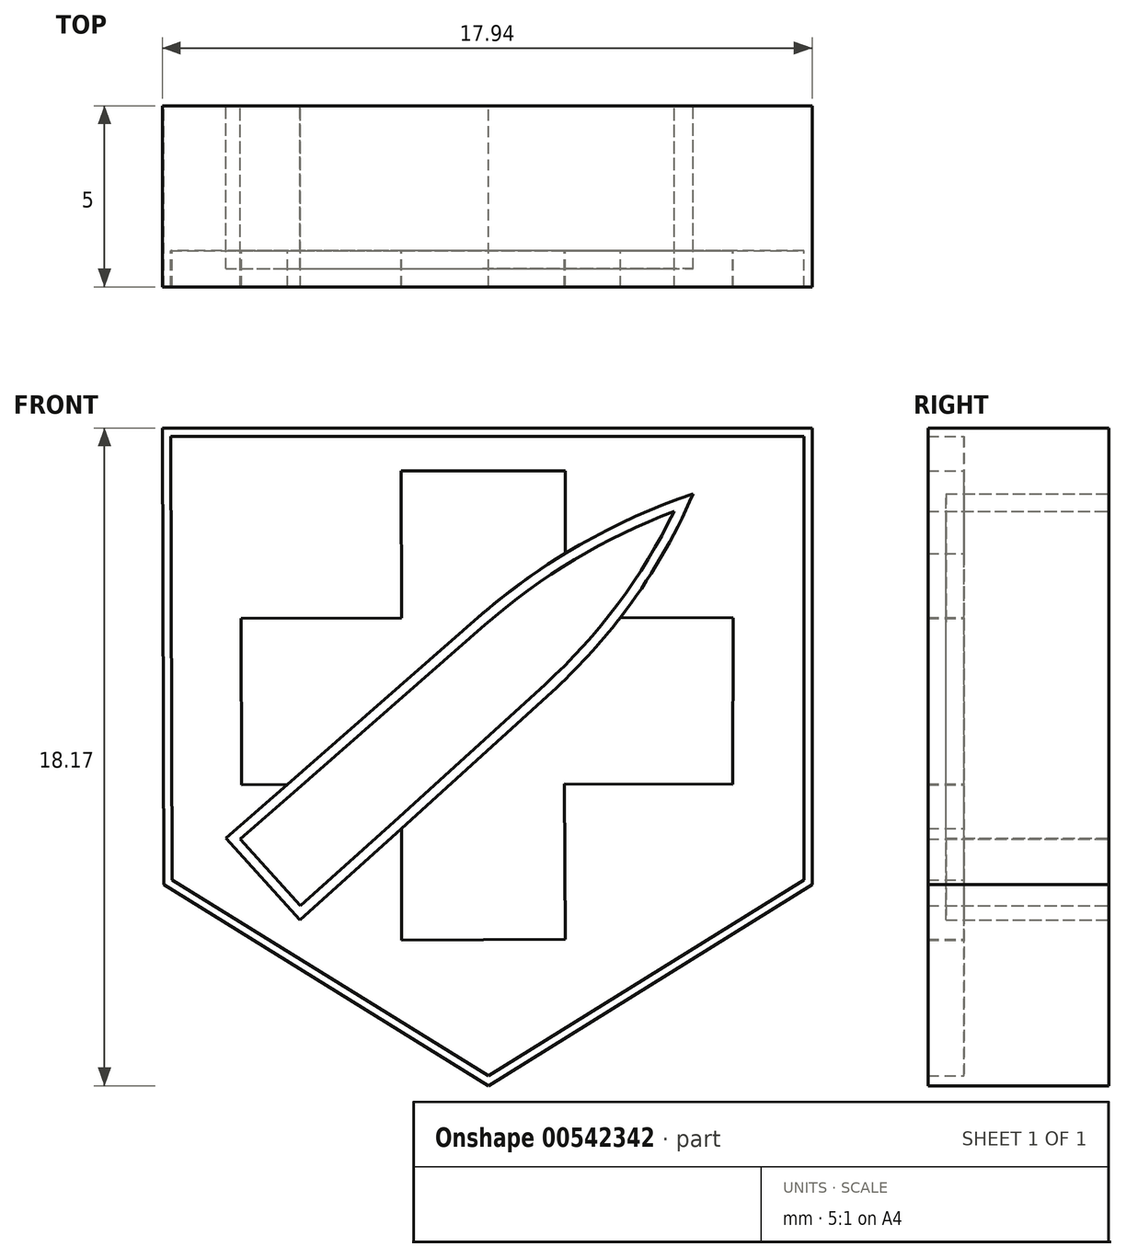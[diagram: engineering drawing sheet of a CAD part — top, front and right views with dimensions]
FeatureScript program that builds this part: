
annotation { "Feature Type Name" : "Feature", "Feature Type Description" : "" }
export const myFeature = defineFeature(function(context is Context, id is Id, definition is map)
    precondition{}
    {
        {
            var Q0;
            Q0=qCreatedBy(makeId("Front.planeOp"),FACE);
            var sketch = newSketch(context, id + "F0", { "sketchPlane" : qUnion([Q0])});
            skLineSegment(sketch, "E0", {"start": v(-10.75, 10.44) * mm, "end": v(7.2, 10.44) * mm});
            skLineSegment(sketch, "E1", {"start": v(7.2, 10.44) * mm, "end": v(7.2, -2.18) * mm});
            skLineSegment(sketch, "E2", {"start": v(7.2, -2.18) * mm, "end": v(-1.75, -7.73) * mm});
            skLineSegment(sketch, "E3", {"start": v(-1.75, -7.73) * mm, "end": v(-10.7, -2.18) * mm});
            skLineSegment(sketch, "E4", {"start": v(-10.7, -2.18) * mm, "end": v(-10.75, 10.44) * mm});
            skLineSegment(sketch, "E5.0", {"start": v(-10.52, 10.22) * mm, "end": v(6.96, 10.22) * mm});
            skLineSegment(sketch, "E5.1", {"start": v(-10.48, -2.05) * mm, "end": v(-10.52, 10.22) * mm});
            skLineSegment(sketch, "E5.2", {"start": v(6.96, 10.22) * mm, "end": v(6.96, -2.05) * mm});
            skLineSegment(sketch, "E5.3", {"start": v(6.96, -2.05) * mm, "end": v(-1.75, -7.46) * mm});
            skLineSegment(sketch, "E5.4", {"start": v(-1.75, -7.46) * mm, "end": v(-10.48, -2.05) * mm});
            skLineSegment(sketch, "E6", {"start": v(-4.17, 9.25) * mm, "end": v(-4.15, 5.2) * mm});
            skLineSegment(sketch, "E7", {"start": v(-4.15, 5.2) * mm, "end": v(-8.58, 5.18) * mm});
            skLineSegment(sketch, "E8", {"start": v(-8.58, 5.18) * mm, "end": v(-8.56, 0.59) * mm});
            skLineSegment(sketch, "E9", {"start": v(-8.56, 0.59) * mm, "end": v(-7.3, 0.6) * mm});
            skLineSegment(sketch, "E10", {"start": v(-7.3, 0.6) * mm, "end": v(-4.15, 0.6) * mm});
            skLineSegment(sketch, "E11", {"start": v(-4.15, -3.7) * mm, "end": v(-4.15, 0.6) * mm});
            skLineSegment(sketch, "E12", {"start": v(-4.15, -3.7) * mm, "end": v(0.37, -3.69) * mm});
            skLineSegment(sketch, "E13", {"start": v(0.37, -3.69) * mm, "end": v(0.35, 0.6) * mm});
            skLineSegment(sketch, "E14", {"start": v(0.35, 0.6) * mm, "end": v(5, 0.6) * mm});
            skLineSegment(sketch, "E15", {"start": v(5, 0.6) * mm, "end": v(5, 5.2) * mm});
            skLineSegment(sketch, "E16", {"start": v(5, 5.2) * mm, "end": v(0.37, 5.2) * mm});
            skLineSegment(sketch, "E17", {"start": v(0.37, 5.2) * mm, "end": v(0.37, 9.25) * mm});
            skLineSegment(sketch, "E18", {"start": v(0.37, 9.25) * mm, "end": v(-4.17, 9.25) * mm});
            skLineSegment(sketch, "E19", {"start": v(-9, -0.89) * mm, "end": v(-6.96, -3.16) * mm});
            skLineSegment(sketch, "E20", {"start": v(-6.96, -3.16) * mm, "end": v(-4.17, -0.64) * mm});
            skLineSegment(sketch, "E21", {"start": v(-9, -0.89) * mm, "end": v(-7.3, 0.6) * mm});
            skLineSegment(sketch, "E22", {"start": v(-7.3, 0.6) * mm, "end": v(-2.03, 5.2) * mm});
            skLineSegment(sketch, "E23", {"start": v(-4.17, -0.64) * mm, "end": v(0, 3.15) * mm});
            skArc(sketch, "E24", {"start": v(-2.03, 5.2) * mm, "mid": v(0.77, 7.21) * mm, "end": v(3.9, 8.63) * mm});
            skArc(sketch, "E25", {"start": v(0, 3.15) * mm, "mid": v(2.25, 5.68) * mm, "end": v(3.9, 8.63) * mm});
            skLineSegment(sketch, "E26.0", {"start": v(-8.6, -0.91) * mm, "end": v(-7.12, 0.38) * mm});
            skLineSegment(sketch, "E26.1", {"start": v(-8.6, -0.91) * mm, "end": v(-6.94, -2.76) * mm});
            skArc(sketch, "E26.2", {"start": v(-1.85, 5) * mm, "mid": v(0.62, 6.8) * mm, "end": v(3.38, 8.14) * mm});
            skArc(sketch, "E26.3", {"start": v(-0.19, 3.36) * mm, "mid": v(1.83, 5.58) * mm, "end": v(3.38, 8.14) * mm});
            skLineSegment(sketch, "E26.4", {"start": v(-4.35, -0.43) * mm, "end": v(-0.19, 3.36) * mm});
            skLineSegment(sketch, "E26.5", {"start": v(-7.12, 0.38) * mm, "end": v(-1.85, 5) * mm});
            skLineSegment(sketch, "E26.6", {"start": v(-6.94, -2.76) * mm, "end": v(-4.35, -0.43) * mm});
            skSolve(sketch);
        }
        {
            var Q0;
            Q0=makeQuery(id+"F0.imprint","IMPRINT",FACE,{"disambiguationData":[TD([[makeQuery(id+"F0.imprint","IMPRINT",EDGE,{"derivedFrom":sQuery(id+"F0.wireOp",EDGE,"E0")}),-1.0]])]});
            extrude(context, id + "F1", {"entities" : qUnion([Q0]), "depth" : 5 * mm, "offsetDistance" : 25.4 * mm});
        }
        {
            var Q0;
            Q0=makeQuery(id+"F0.imprint","IMPRINT",FACE,{"disambiguationData":[TD([[makeQuery(id+"F0.imprint","IMPRINT",EDGE,{"derivedFrom":sQuery(id+"F0.wireOp",EDGE,"E5.0")}),-1.0]])]});
            extrude(context, id + "F2", {"entities" : qUnion([Q0]), "operationType" : NewBodyOperationType.ADD, "depth" : 4 * mm, "offsetDistance" : 25.4 * mm});
        }
        {
            var Q0;
            Q0=makeQuery(id+"F0.imprint","IMPRINT",FACE,{"disambiguationData":[TD([[makeQuery(id+"F0.imprint","IMPRINT",EDGE,{"derivedFrom":sQuery(id+"F0.wireOp",EDGE,"E6")}),1.0]])]});
            var Q1;
            {var subQ0=sQuery(id+"F0.wireOp",EDGE,"E12");Q1=makeQuery(id+"F0.imprint","IMPRINT",FACE,{"disambiguationData":[TD([[makeQuery(id+"F0.imprint","IMPRINT",EDGE,{"derivedFrom":subQ0}),1.0]])]});}
            extrude(context, id + "F3", {"entities" : qUnion([Q0, Q1]), "operationType" : NewBodyOperationType.ADD, "depth" : 5 * mm, "offsetDistance" : 25.4 * mm});
        }
        {
            var Q0;
            {var subQ5=sQuery(id+"F0.wireOp",EDGE,"E26.0");Q0=makeQuery(id+"F0.imprint","IMPRINT",FACE,{"disambiguationData":[TD([[makeQuery(id+"F0.imprint","IMPRINT",EDGE,{"derivedFrom":subQ5}),-1.0]])]});}
            var Q1;
            {var subQ5=sQuery(id+"F0.wireOp",EDGE,"E11");var subQ6=sQuery(id+"F0.wireOp",EDGE,"E10");var subQ7=makeQuery(id+"F0.imprint","INTERSECT",VERTEX,{"derivedFrom":[subQ6,subQ5]});Q1=makeQuery(id+"F0.imprint","IMPRINT",FACE,{"disambiguationData":[TD([[makeQuery(id+"F0.imprint","IMPRINT",EDGE,{"disambiguationData":[TD([[subQ7,1.0]])],"derivedFrom":subQ6}),1.0]])]});}
            var Q2;
            {var subQ0=sQuery(id+"F0.wireOp",EDGE,"E17");var subQ1=sQuery(id+"F0.wireOp",EDGE,"E16");var subQ2=makeQuery(id+"F0.imprint","INTERSECT",VERTEX,{"derivedFrom":[subQ1,subQ0]});Q2=makeQuery(id+"F0.imprint","IMPRINT",FACE,{"disambiguationData":[TD([[makeQuery(id+"F0.imprint","IMPRINT",EDGE,{"disambiguationData":[TD([[subQ2,1.0]])],"derivedFrom":subQ1}),-1.0]])]});}
            extrude(context, id + "F4", {"entities" : qUnion([Q0, Q1, Q2]), "depth" : 5 * mm, "offsetDistance" : 25.4 * mm});
        }
        {
            var Q0;
            {var subQ1=sQuery(id+"F0.wireOp",EDGE,"E22");Q0=makeQuery(id+"F0.imprint","IMPRINT",FACE,{"disambiguationData":[TD([[makeQuery(id+"F0.imprint","IMPRINT",EDGE,{"derivedFrom":subQ1}),-1.0]])]});}
            var Q1;
            Q1=makeQuery(id+"F0.imprint","IMPRINT",FACE,{"disambiguationData":[TD([[makeQuery(id+"F0.imprint","IMPRINT",EDGE,{"derivedFrom":sQuery(id+"F0.wireOp",EDGE,"E19")}),1.0]])]});
            var Q2;
            {var subQ1=sQuery(id+"F0.wireOp",EDGE,"E23");var subQ5=sQuery(id+"F0.wireOp",EDGE,"E11");var subQ6=makeQuery(id+"F0.imprint","INTERSECT",VERTEX,{"derivedFrom":[subQ5,subQ1]});Q2=makeQuery(id+"F0.imprint","IMPRINT",FACE,{"disambiguationData":[TD([[makeQuery(id+"F0.imprint","IMPRINT",EDGE,{"disambiguationData":[TD([[subQ6,-1.0]])],"derivedFrom":subQ5}),-1.0]])]});}
            var Q3;
            {var subQ0=sQuery(id+"F0.wireOp",EDGE,"E25");var subQ7=sQuery(id+"F0.wireOp",EDGE,"E16");var subQ8=makeQuery(id+"F0.imprint","INTERSECT",VERTEX,{"derivedFrom":[subQ7,subQ0]});Q3=makeQuery(id+"F0.imprint","IMPRINT",FACE,{"disambiguationData":[TD([[makeQuery(id+"F0.imprint","IMPRINT",EDGE,{"disambiguationData":[TD([[subQ8,-1.0]])],"derivedFrom":subQ7}),-1.0]])]});}
            extrude(context, id + "F5", {"entities" : qUnion([Q0, Q1, Q2, Q3]), "depth" : 4.5 * mm, "offsetDistance" : 25.4 * mm});
        }
    });
